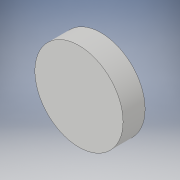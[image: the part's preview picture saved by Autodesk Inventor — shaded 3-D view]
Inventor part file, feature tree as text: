
AUTODESK INVENTOR PART (.ipt)
format: ipt  version: 2017 (Build 210142000, 142)  size: 90,112 bytes
history: native  units: in
note: dims shown in document units (in); Inventor stores cm internally (conversion verified against a paired STEP export)
features: extrude x1, sketch x1
ambient origin geometry x8: Origin, YZ Plane, XZ Plane, XY Plane, X Axis, Y Axis, Z Axis, Center Point
bodies: Solid1 (feature_tree)
feature tree (2):
  extrude  "Extrusion1"  Depth=0.5in TaperAngle=0.0deg
  sketch  "Sketch1"  dims[d0=2.0in d1=0.5in d2=0.0in]
